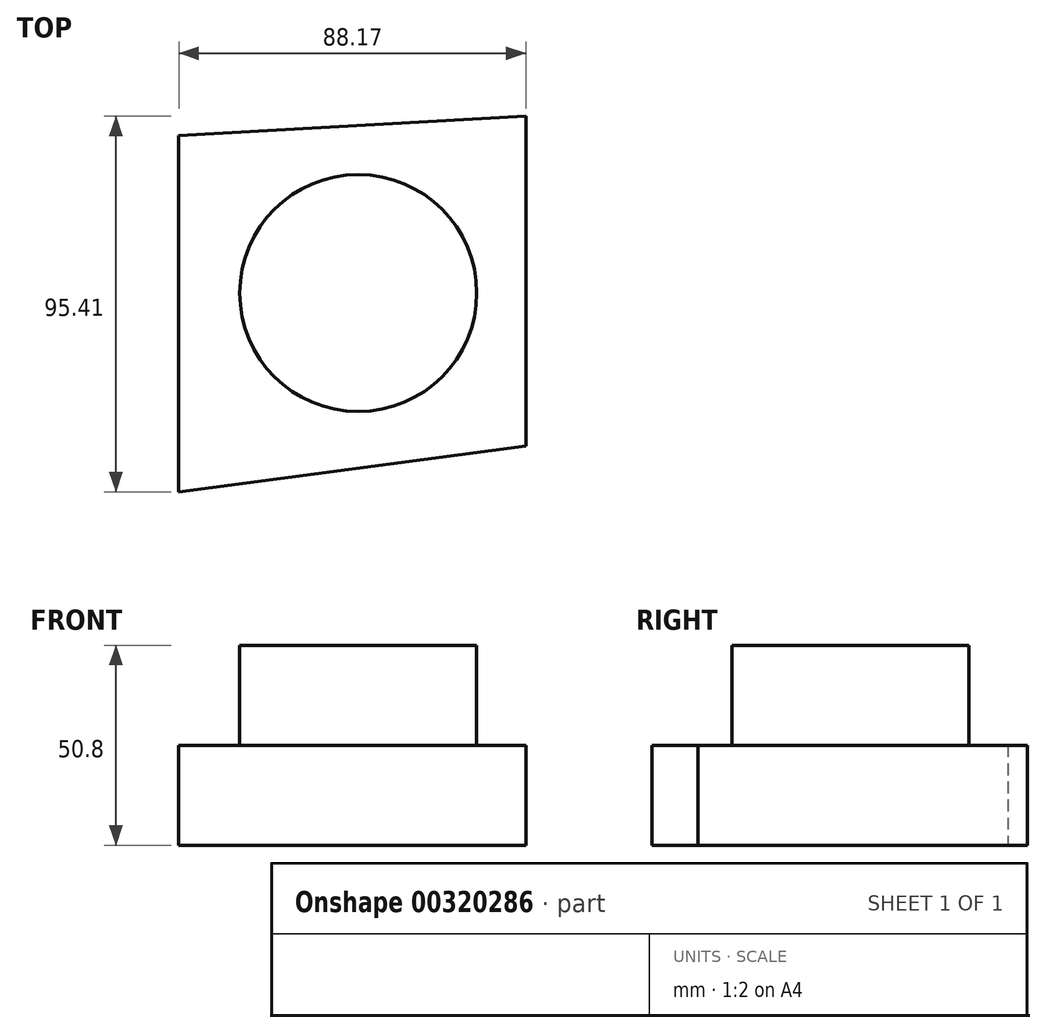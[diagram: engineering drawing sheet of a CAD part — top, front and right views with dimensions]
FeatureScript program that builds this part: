
annotation { "Feature Type Name" : "Feature", "Feature Type Description" : "" }
export const myFeature = defineFeature(function(context is Context, id is Id, definition is map)
    precondition{}
    {
        {
            var Q0;
            Q0=qCreatedBy(makeId("Top.planeOp"),FACE);
            var sketch = newSketch(context, id + "F0", { "sketchPlane" : qUnion([Q0])});
            skLineSegment(sketch, "E0", {"start": v(-88.17, 39.97) * mm, "end": v(-88.17, -50.5) * mm});
            skLineSegment(sketch, "E1", {"start": v(-88.17, -50.5) * mm, "end": v(0, -38.81) * mm});
            skLineSegment(sketch, "E2", {"start": v(0, -38.81) * mm, "end": v(0, 44.92) * mm});
            skLineSegment(sketch, "E3", {"start": v(0, 44.92) * mm, "end": v(-88.17, 39.97) * mm});
            skSolve(sketch);
        }
        {
            var Q0;
            Q0 = qSketchRegion(id + "F0", true);
            extrude(context, id + "F1", {"entities" : qUnion([Q0]), "depth" : 25.4 * mm});
        }
        {
            var Q0;
            Q0=makeQuery(id+"F1.opExtrude","CAP_FACE",FACE,{"disambiguationData":[OSD([sQuery(id+"F0.wireOp",EDGE,"E0"),sQuery(id+"F0.wireOp",EDGE,"E1"),sQuery(id+"F0.wireOp",EDGE,"E2"),sQuery(id+"F0.wireOp",EDGE,"E3")])],"isStart":false});
            var sketch = newSketch(context, id + "F2", { "sketchPlane" : qUnion([Q0])});
            skCircle(sketch, "E4", {"center": v(-42.6, 0) * mm, "radius": 30.1 * mm});
            skSolve(sketch);
        }
        {
            var Q0;
            Q0 = qSketchRegion(id + "F2", true);
            extrude(context, id + "F3", {"entities" : qUnion([Q0]), "operationType" : NewBodyOperationType.ADD, "depth" : 25.4 * mm});
        }
    });
